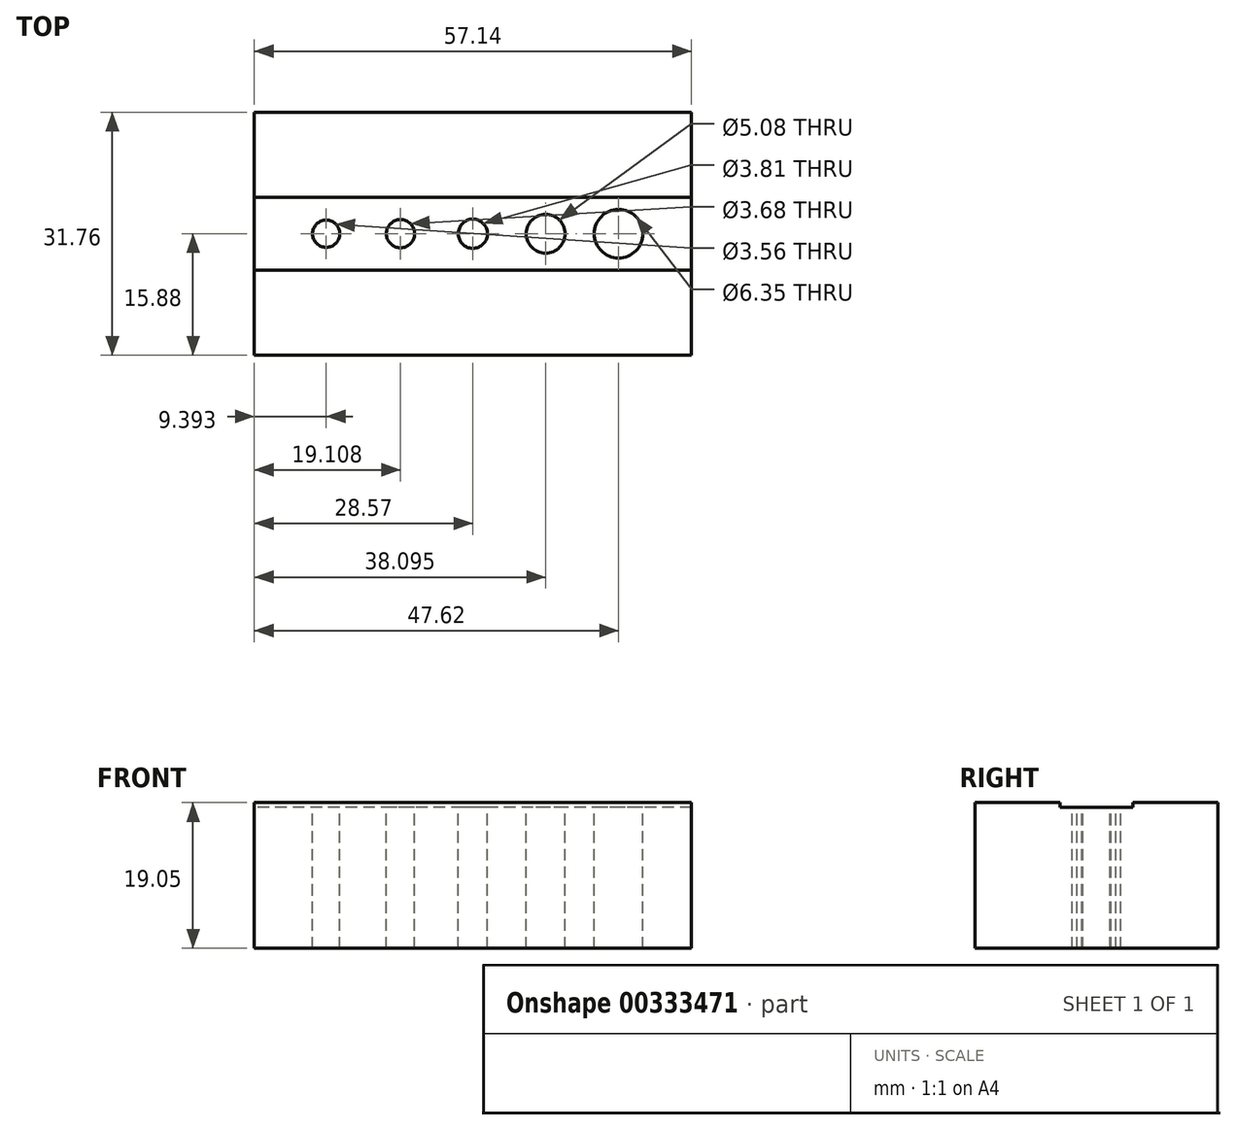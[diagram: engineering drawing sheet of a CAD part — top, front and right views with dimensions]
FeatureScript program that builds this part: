
annotation { "Feature Type Name" : "Feature", "Feature Type Description" : "" }
export const myFeature = defineFeature(function(context is Context, id is Id, definition is map)
    precondition{}
    {
        {
            var Q0;
            Q0=qCreatedBy(makeId("Top.planeOp"),FACE);
            var sketch = newSketch(context, id + "F0", { "sketchPlane" : qUnion([Q0])});
            skLineSegment(sketch, "E0.bottom", {"start": v(28.57, 15.88) * mm, "end": v(-28.58, 15.87) * mm});
            skLineSegment(sketch, "E0.top", {"start": v(28.58, -15.87) * mm, "end": v(-28.57, -15.88) * mm});
            skLineSegment(sketch, "E0.left", {"start": v(28.57, 15.88) * mm, "end": v(28.58, -15.87) * mm});
            skLineSegment(sketch, "E0.right", {"start": v(-28.58, 15.87) * mm, "end": v(-28.57, -15.88) * mm});
            skPoint(sketch, "E0.middle", {"position": v(0, 0) * mm});
            skLineSegment(sketch, "E1.bottom", {"start": v(28.58, 4.76) * mm, "end": v(-28.58, 4.76) * mm});
            skLineSegment(sketch, "E1.top", {"start": v(28.58, -4.76) * mm, "end": v(-28.58, -4.76) * mm});
            skLineSegment(sketch, "E1.left", {"start": v(28.57, 4.76) * mm, "end": v(28.57, -4.76) * mm});
            skLineSegment(sketch, "E1.right", {"start": v(-28.57, 4.76) * mm, "end": v(-28.57, -4.76) * mm});
            skCircle(sketch, "E2", {"center": v(19.05, 0) * mm, "radius": 3.18 * mm});
            skCircle(sketch, "E3", {"center": v(9.52, 0) * mm, "radius": 2.54 * mm});
            skCircle(sketch, "E4", {"center": v(0, 0) * mm, "radius": 1.9 * mm});
            skCircle(sketch, "E5", {"center": v(-9.46, 0) * mm, "radius": 1.84 * mm});
            skCircle(sketch, "E6", {"center": v(-19.18, 0) * mm, "radius": 1.78 * mm});
            skSolve(sketch);
        }
        {
            var Q0;
            {var subQ0=sQuery(id+"F0.wireOp",EDGE,"E0.bottom");Q0=makeQuery(id+"F0.imprint","IMPRINT",FACE,{"disambiguationData":[TD([[makeQuery(id+"F0.imprint","IMPRINT",EDGE,{"derivedFrom":subQ0}),1.0]])]});}
            var Q1;
            Q1=makeQuery(id+"F0.imprint","IMPRINT",FACE,{"disambiguationData":[TD([[makeQuery(id+"F0.imprint","IMPRINT",EDGE,{"derivedFrom":sQuery(id+"F0.wireOp",EDGE,"E1.bottom")}),1.0]])]});
            var Q2;
            {var subQ0=sQuery(id+"F0.wireOp",EDGE,"E0.top");Q2=makeQuery(id+"F0.imprint","IMPRINT",FACE,{"disambiguationData":[TD([[makeQuery(id+"F0.imprint","IMPRINT",EDGE,{"derivedFrom":subQ0}),-1.0]])]});}
            extrude(context, id + "F1", {"entities" : qUnion([Q0, Q1, Q2]), "oppositeDirection" : true, "depth" : 19.05 * mm});
        }
        {
            var Q0;
            Q0=makeQuery(id+"F0.imprint","IMPRINT",FACE,{"disambiguationData":[TD([[makeQuery(id+"F0.imprint","IMPRINT",EDGE,{"derivedFrom":sQuery(id+"F0.wireOp",EDGE,"E1.bottom")}),1.0]])]});
            extrude(context, id + "F2", {"entities" : qUnion([Q0]), "operationType" : NewBodyOperationType.REMOVE, "oppositeDirection" : true, "depth" : 0.64 * mm});
        }
    });
